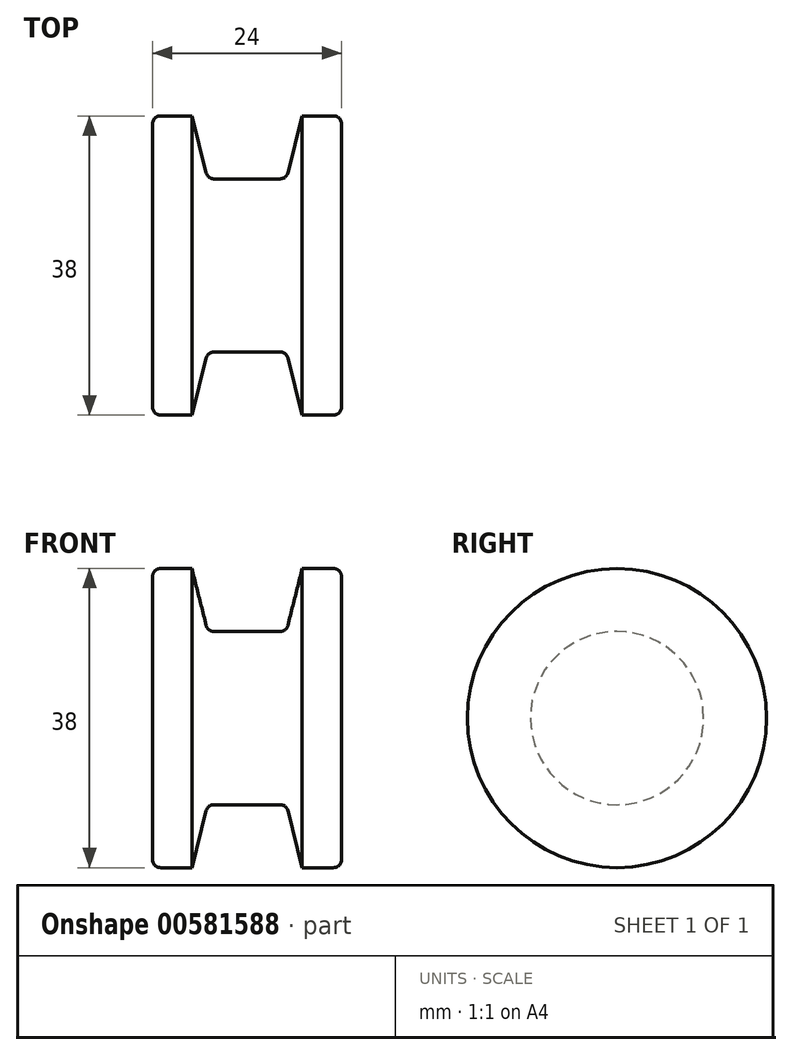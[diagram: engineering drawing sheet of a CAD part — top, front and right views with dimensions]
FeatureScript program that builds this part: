
annotation { "Feature Type Name" : "Feature", "Feature Type Description" : "" }
export const myFeature = defineFeature(function(context is Context, id is Id, definition is map)
    precondition{}
    {
        {
            var Q0;
            Q0=qCreatedBy(makeId("Top.planeOp"),FACE);
            var sketch = newSketch(context, id + "F0", { "sketchPlane" : qUnion([Q0])});
            skLineSegment(sketch, "E0.bottom", {"start": v(-12, 0) * mm, "end": v(12, 0) * mm});
            skLineSegment(sketch, "E0.top", {"start": v(-12, 23) * mm, "end": v(12, 23) * mm});
            skLineSegment(sketch, "E0.left", {"start": v(-12, 0) * mm, "end": v(-12, 23) * mm});
            skLineSegment(sketch, "E0.right", {"start": v(12, 0) * mm, "end": v(12, 23) * mm});
            skLineSegment(sketch, "E1.bottom", {"start": v(12, 19) * mm, "end": v(7, 19) * mm});
            skLineSegment(sketch, "E1.top", {"start": v(12, 0) * mm, "end": v(8, 0) * mm});
            skLineSegment(sketch, "E1.left", {"start": v(12, 19) * mm, "end": v(12, 0) * mm});
            skLineSegment(sketch, "E2.bottom", {"start": v(-12, 19) * mm, "end": v(-7, 19) * mm});
            skLineSegment(sketch, "E2.top", {"start": v(-12, 0) * mm, "end": v(-8, 0) * mm});
            skLineSegment(sketch, "E2.left", {"start": v(-12, 19) * mm, "end": v(-12, 0) * mm});
            skLineSegment(sketch, "E3.bottom", {"start": v(-2.5, 23) * mm, "end": v(2.5, 23) * mm});
            skLineSegment(sketch, "E3.top", {"start": v(-2.5, 15) * mm, "end": v(2.5, 15) * mm});
            skLineSegment(sketch, "E3.left", {"start": v(-2.5, 23) * mm, "end": v(-2.5, 15) * mm});
            skLineSegment(sketch, "E3.right", {"start": v(2.5, 23) * mm, "end": v(2.5, 15) * mm});
            skLineSegment(sketch, "E4", {"start": v(-5, 11) * mm, "end": v(5, 11) * mm});
            skLineSegment(sketch, "E5", {"start": v(-5, 11) * mm, "end": v(-7, 19) * mm});
            skLineSegment(sketch, "E6", {"start": v(7, 19) * mm, "end": v(5, 11) * mm});
            skLineSegment(sketch, "E7", {"start": v(5, 11) * mm, "end": v(5, 10) * mm});
            skLineSegment(sketch, "E8", {"start": v(5, 10) * mm, "end": v(3.5, 10) * mm});
            skLineSegment(sketch, "E9", {"start": v(3.5, 10) * mm, "end": v(3.5, 11) * mm});
            skSolve(sketch);
        }
        {
            var Q0;
            {var subQ5=sQuery(id+"F0.wireOp",EDGE,"E0.left");Q0=makeQuery(id+"F0.imprint","IMPRINT",FACE,{"disambiguationData":[TD([[makeQuery(id+"F0.imprint","IMPRINT",EDGE,{"derivedFrom":subQ5}),-1.0]])]});}
            var Q1;
            {var subQ0=sQuery(id+"F0.wireOp",EDGE,"E7");Q1=makeQuery(id+"F0.imprint","IMPRINT",FACE,{"disambiguationData":[TD([[makeQuery(id+"F0.imprint","IMPRINT",EDGE,{"derivedFrom":subQ0}),-1.0]])]});}
            var Q2;
            Q2=sQuery(id+"F0.wireOp",EDGE,"E0.bottom");
            revolve(context, id + "F1", {"entities" : qUnion([Q0, Q1]), "axis" : qUnion([Q2]), "revolveType" : RevolveType.FULL, "surfaceOperationType" : NewSurfaceOperationType.NEW});
        }
        {
            var Q0;
            Q0=makeQuery(id+"F1.opRevolve","SWEPT_EDGE",EDGE,{"disambiguationData":[OSD([sQuery(id+"F0.wireOp",EDGE,"E0.top"),sQuery(id+"F0.wireOp",EDGE,"E0.left")])]});
            var Q1;
            Q1=makeQuery(id+"F1.opRevolve","SWEPT_EDGE",EDGE,{"disambiguationData":[OSD([sQuery(id+"F0.wireOp",EDGE,"E0.top"),sQuery(id+"F0.wireOp",EDGE,"E3.bottom"),sQuery(id+"F0.wireOp",EDGE,"E3.left")])]});
            var Q2;
            Q2=makeQuery(id+"F1.opRevolve","SWEPT_EDGE",EDGE,{"disambiguationData":[OSD([sQuery(id+"F0.wireOp",EDGE,"E0.top"),sQuery(id+"F0.wireOp",EDGE,"E3.bottom"),sQuery(id+"F0.wireOp",EDGE,"E3.right")])]});
            var Q3;
            Q3=makeQuery(id+"F1.opRevolve","SWEPT_EDGE",EDGE,{"disambiguationData":[OSD([sQuery(id+"F0.wireOp",EDGE,"E0.top"),sQuery(id+"F0.wireOp",EDGE,"E0.right")])]});
            var Q4;
            Q4=makeQuery(id+"F1.opRevolve","SWEPT_EDGE",EDGE,{"disambiguationData":[OSD([sQuery(id+"F0.wireOp",EDGE,"E3.top"),sQuery(id+"F0.wireOp",EDGE,"E3.right")])]});
            var Q5;
            Q5=makeQuery(id+"F1.opRevolve","SWEPT_EDGE",EDGE,{"disambiguationData":[OSD([sQuery(id+"F0.wireOp",EDGE,"E3.top"),sQuery(id+"F0.wireOp",EDGE,"E3.left")])]});
            var Q6;
            Q6=makeQuery(id+"F1.opRevolve","SWEPT_EDGE",EDGE,{"disambiguationData":[OSD([sQuery(id+"F0.wireOp",EDGE,"E4"),sQuery(id+"F0.wireOp",EDGE,"E5")])]});
            var Q7;
            Q7=makeQuery(id+"F1.opRevolve","SWEPT_EDGE",EDGE,{"disambiguationData":[OSD([sQuery(id+"F0.wireOp",EDGE,"E7"),sQuery(id+"F0.wireOp",EDGE,"E8")])]});
            fillet(context, id + "F2", {"entities" : qUnion([Q0, Q1, Q2, Q3, Q4, Q5, Q6, Q7]), "radius" : 1 * mm, "tangentPropagation" : true, "allowEdgeOverflow" : false});
        }
    });
